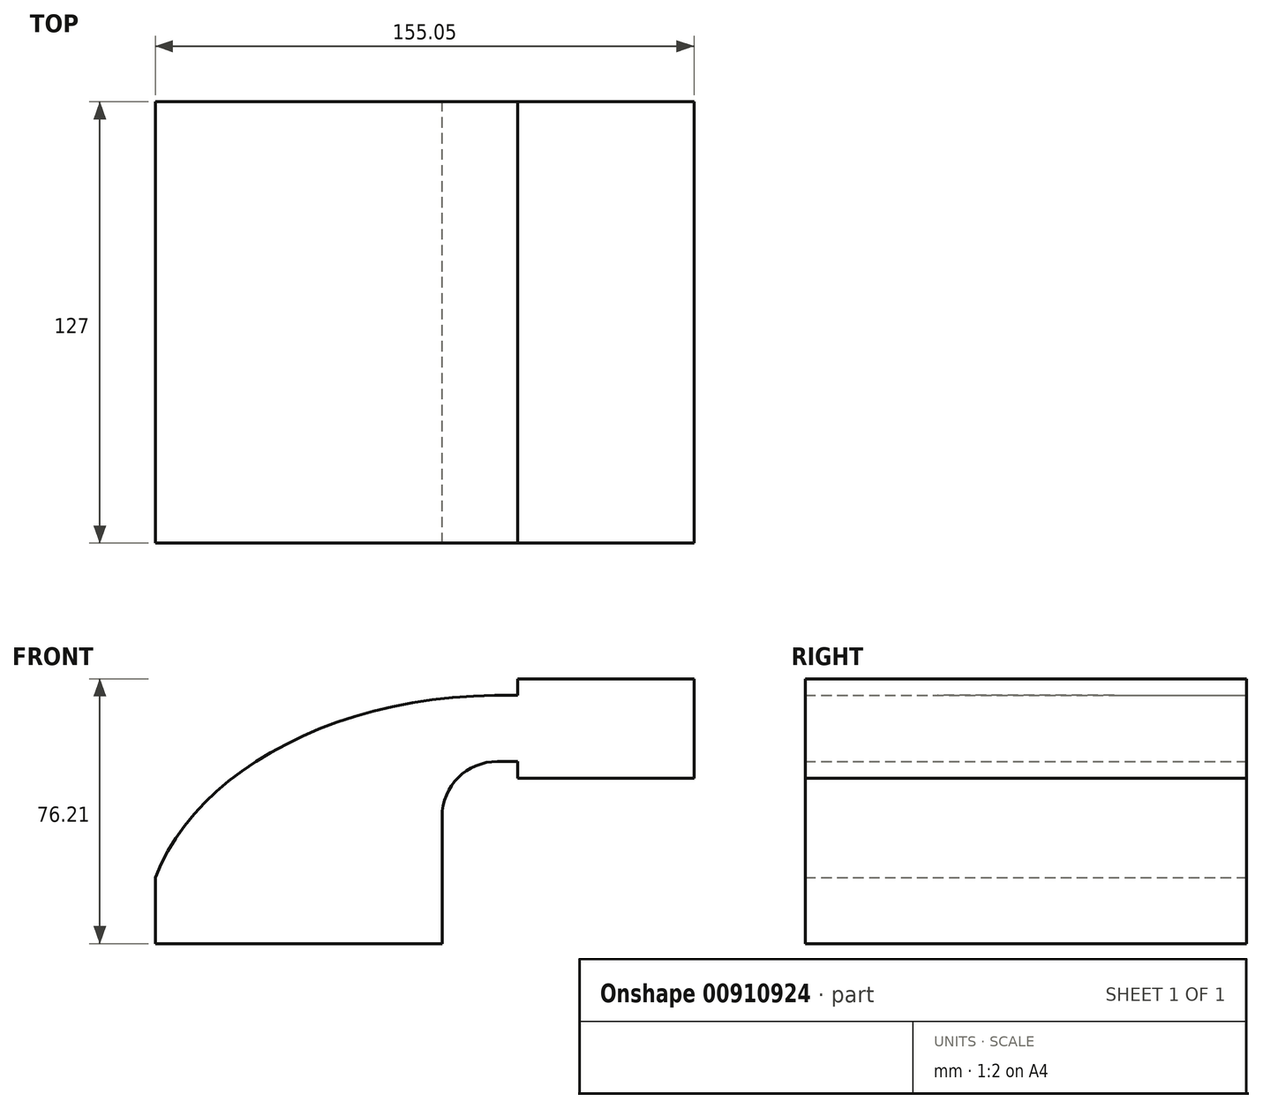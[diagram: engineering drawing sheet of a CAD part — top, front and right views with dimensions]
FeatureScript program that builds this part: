
annotation { "Feature Type Name" : "Feature", "Feature Type Description" : "" }
export const myFeature = defineFeature(function(context is Context, id is Id, definition is map)
    precondition{}
    {
        {
            var Q0;
            Q0=qCreatedBy(makeId("Front.planeOp"),FACE);
            var sketch = newSketch(context, id + "F0", { "sketchPlane" : qUnion([Q0])});
            skLineSegment(sketch, "E0.bottom", {"start": v(-41.28, 9.52) * mm, "end": v(41.27, 9.53) * mm});
            skLineSegment(sketch, "E0.top", {"start": v(-41.28, -9.53) * mm, "end": v(41.28, -9.53) * mm});
            skLineSegment(sketch, "E0.left", {"start": v(-41.28, 9.52) * mm, "end": v(-41.28, -9.53) * mm});
            skLineSegment(sketch, "E0.right", {"start": v(41.27, 9.53) * mm, "end": v(41.28, -9.52) * mm});
            skPoint(sketch, "E0.middle", {"position": v(0, 0) * mm});
            skLineSegment(sketch, "E1.bottom", {"start": v(62.97, 38.1) * mm, "end": v(113.77, 38.1) * mm});
            skLineSegment(sketch, "E1.top", {"start": v(62.97, 66.68) * mm, "end": v(113.77, 66.68) * mm});
            skLineSegment(sketch, "E1.left", {"start": v(62.97, 38.1) * mm, "end": v(62.97, 66.68) * mm});
            skLineSegment(sketch, "E1.right", {"start": v(113.77, 38.1) * mm, "end": v(113.77, 66.68) * mm});
            skPoint(sketch, "E1.middle", {"position": v(88.37, 52.39) * mm});
            skLineSegment(sketch, "E2", {"start": v(41.27, 9.53) * mm, "end": v(41.27, 27) * mm});
            skArc(sketch, "E3", {"start": v(41.27, 27) * mm, "mid": v(45.92, 38.23) * mm, "end": v(57.15, 42.88) * mm});
            skLineSegment(sketch, "E4", {"start": v(57.15, 42.88) * mm, "end": v(88.37, 42.88) * mm});
            skPoint(sketch, "E4.endSnap0", {"position": v(88.37, 38.1) * mm});
            skLineSegment(sketch, "E5.0", {"start": v(57.15, 61.93) * mm, "end": v(88.37, 61.93) * mm});
            skArc(sketch, "E5.1", {"start": v(22.22, 27) * mm, "mid": v(32.45, 51.7) * mm, "end": v(57.15, 61.93) * mm});
            skLineSegment(sketch, "E5.2", {"start": v(22.22, 9.53) * mm, "end": v(22.22, 27) * mm});
            skLineSegment(sketch, "E6", {"start": v(88.37, 38.1) * mm, "end": v(88.37, 66.68) * mm});
            skFitSpline(sketch, "E7", {"points": [v(-41.28, 9.52) * mm, v(57.15, 61.93) * mm], "startDerivative": vector(34.4, 89.93) * mm, "endDerivative": vector(142.7, 1.1) * mm});
            skSolve(sketch);
        }
        {
            var Q0;
            {var subQ4=sQuery(id+"F0.wireOp",EDGE,"E1.right");Q0=makeQuery(id+"F0.imprint","IMPRINT",FACE,{"disambiguationData":[TD([[makeQuery(id+"F0.imprint","IMPRINT",EDGE,{"derivedFrom":subQ4}),1.0]])]});}
            var Q1;
            {var subQ0=sQuery(id+"F0.wireOp",EDGE,"E4");var subQ1=sQuery(id+"F0.wireOp",EDGE,"E1.left");var subQ2=makeQuery(id+"F0.imprint","INTERSECT",VERTEX,{"derivedFrom":[subQ1,subQ0]});Q1=makeQuery(id+"F0.imprint","IMPRINT",FACE,{"disambiguationData":[TD([[makeQuery(id+"F0.imprint","IMPRINT",EDGE,{"disambiguationData":[TD([[subQ2,-1.0]])],"derivedFrom":subQ1}),-1.0]])]});}
            var Q2;
            {var subQ0=sQuery(id+"F0.wireOp",EDGE,"E1.left");var subQ1=sQuery(id+"F0.wireOp",EDGE,"E1.top");var subQ2=makeQuery(id+"F0.imprint","INTERSECT",VERTEX,{"derivedFrom":[subQ1,subQ0]});Q2=makeQuery(id+"F0.imprint","IMPRINT",FACE,{"disambiguationData":[TD([[makeQuery(id+"F0.imprint","IMPRINT",EDGE,{"disambiguationData":[TD([[subQ2,-1.0]])],"derivedFrom":subQ1}),-1.0]])]});}
            var Q3;
            {var subQ0=sQuery(id+"F0.wireOp",EDGE,"E1.left");var subQ1=sQuery(id+"F0.wireOp",EDGE,"E1.bottom");var subQ2=makeQuery(id+"F0.imprint","INTERSECT",VERTEX,{"derivedFrom":[subQ1,subQ0]});Q3=makeQuery(id+"F0.imprint","IMPRINT",FACE,{"disambiguationData":[TD([[makeQuery(id+"F0.imprint","IMPRINT",EDGE,{"disambiguationData":[TD([[subQ2,-1.0]])],"derivedFrom":subQ1}),1.0]])]});}
            var Q4;
            {var subQ1=sQuery(id+"F0.wireOp",EDGE,"E2");Q4=makeQuery(id+"F0.imprint","IMPRINT",FACE,{"disambiguationData":[TD([[makeQuery(id+"F0.imprint","IMPRINT",EDGE,{"derivedFrom":subQ1}),1.0]])]});}
            extrude(context, id + "F1", {"entities" : qUnion([Q0, Q1, Q2, Q3, Q4]), "endBound" : BoundingType.SYMMETRIC, "depth" : 50.8 * mm, "offsetDistance" : 25.4 * mm});
        }
        {
            var Q0;
            Q0 = qSketchRegion(id + "F0", true);
            extrude(context, id + "F2", {"entities" : qUnion([Q0]), "operationType" : NewBodyOperationType.ADD, "endBound" : BoundingType.SYMMETRIC, "depth" : 127 * mm, "offsetDistance" : 25.4 * mm});
        }
    });
